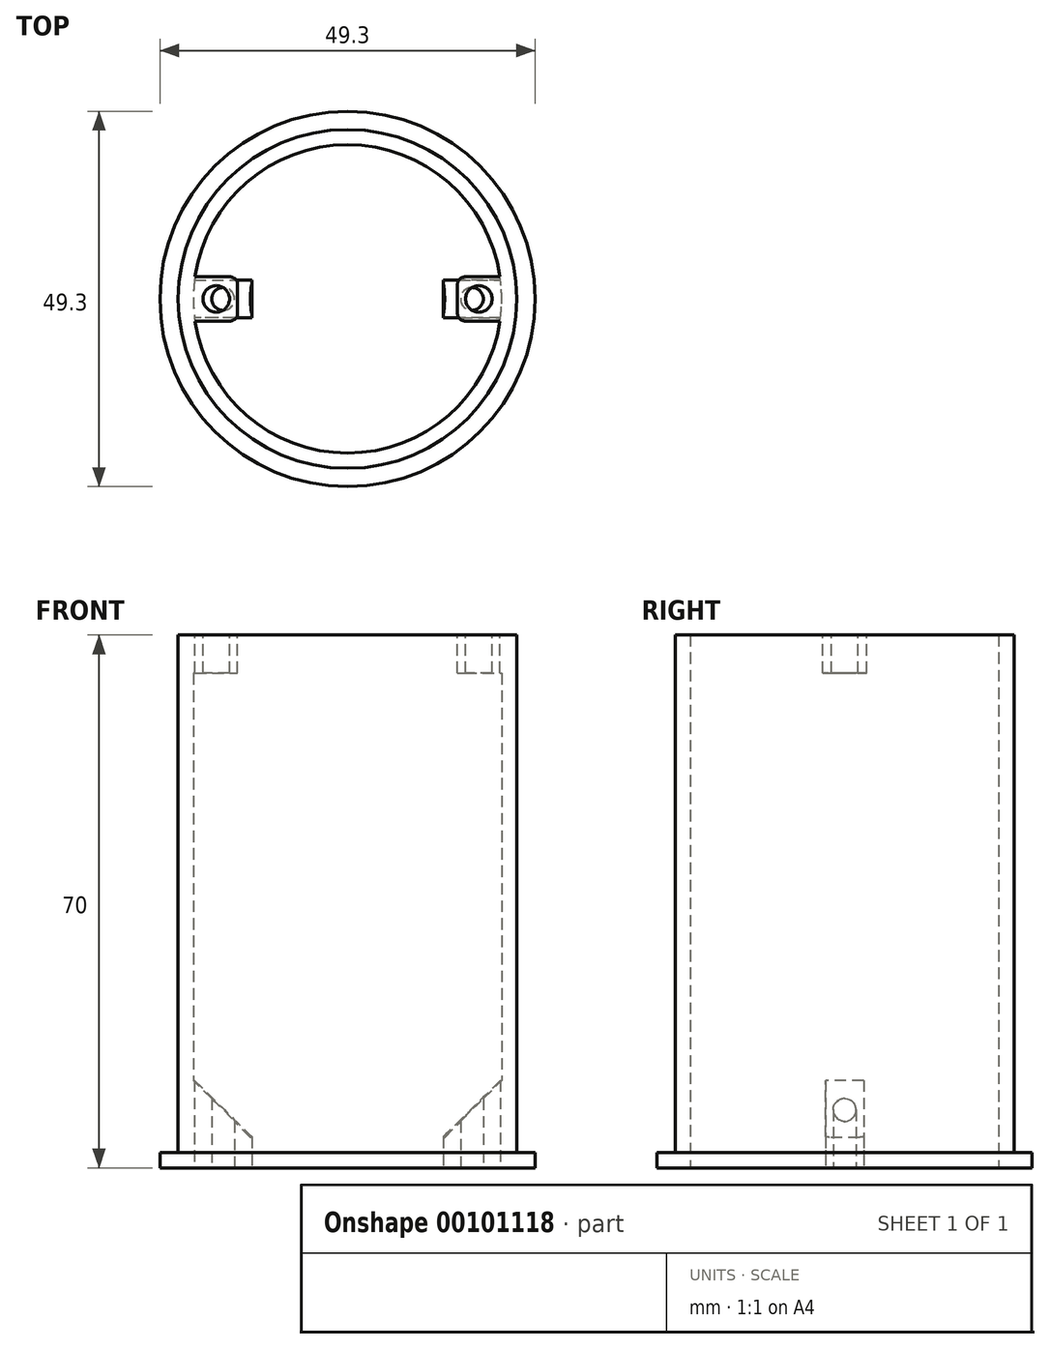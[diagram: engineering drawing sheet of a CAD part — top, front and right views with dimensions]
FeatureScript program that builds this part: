
annotation { "Feature Type Name" : "Feature", "Feature Type Description" : "" }
export const myFeature = defineFeature(function(context is Context, id is Id, definition is map)
    precondition{}
    {
        {
            var Q0;
            Q0=qCreatedBy(makeId("Top.planeOp"),FACE);
            var sketch = newSketch(context, id + "F0", { "sketchPlane" : qUnion([Q0])});
            skLineSegment(sketch, "E0.bottom", {"start": v(-4, 4) * mm, "end": v(4, 4) * mm});
            skLineSegment(sketch, "E0.top", {"start": v(-4, -4) * mm, "end": v(4, -4) * mm});
            skLineSegment(sketch, "E0.left", {"start": v(-4, 4) * mm, "end": v(-4, -4) * mm});
            skLineSegment(sketch, "E0.right", {"start": v(4, 4) * mm, "end": v(4, -4) * mm});
            skPoint(sketch, "E0.middle", {"position": v(0, 0) * mm});
            skLineSegment(sketch, "E1.bottom", {"start": v(-11, 11) * mm, "end": v(11, 11) * mm});
            skLineSegment(sketch, "E1.top", {"start": v(-11, -11) * mm, "end": v(11, -11) * mm});
            skLineSegment(sketch, "E1.left", {"start": v(-11, 11) * mm, "end": v(-11, -11) * mm});
            skLineSegment(sketch, "E1.right", {"start": v(11, 11) * mm, "end": v(11, -11) * mm});
            skCircle(sketch, "E2", {"center": v(0, 0) * mm, "radius": 10 * mm});
            skPoint(sketch, "E3", {"position": v(-7.5, 0) * mm});
            skPoint(sketch, "E3.positionSnap0", {"position": v(-11, 0) * mm});
            skCircle(sketch, "E4", {"center": v(-7.5, 0) * mm, "radius": 1.5 * mm});
            skPoint(sketch, "E5", {"position": v(7.5, 0) * mm});
            skPoint(sketch, "E5.positionSnap0", {"position": v(11, 0) * mm});
            skCircle(sketch, "E6", {"center": v(7.5, 0) * mm, "radius": 1.5 * mm});
            skCircle(sketch, "E7", {"center": v(0, 0) * mm, "radius": 22.25 * mm});
            skCircle(sketch, "E8", {"center": v(0, 0) * mm, "radius": 20.25 * mm});
            skSolve(sketch);
        }
        {
            var Q0;
            Q0=makeQuery(id+"F0.imprint","IMPRINT",FACE,{"disambiguationData":[TD([[makeQuery(id+"F0.imprint","IMPRINT",EDGE,{"derivedFrom":sQuery(id+"F0.wireOp",EDGE,"E7")}),1.0]])]});
            extrude(context, id + "F1", {"entities" : qUnion([Q0]), "depth" : 70 * mm});
        }
        {
            var Q0;
            Q0=makeQuery(id+"F1.opExtrude","CAP_FACE",FACE,{"disambiguationData":[OSD([sQuery(id+"F0.wireOp",EDGE,"E7"),sQuery(id+"F0.wireOp",EDGE,"E8")])],"isStart":false});
            cPlane(context, id + "F2", {"entities" : qUnion([Q0]), "cplaneType" : CPlaneType.OFFSET, "offset" : 0 * mm, "width" : 150 * mm, "height" : 150 * mm});
        }
        {
            var Q0;
            Q0=qCreatedBy(id+"F2.planeOp",FACE);
            var sketch = newSketch(context, id + "F3", { "sketchPlane" : qUnion([Q0])});
            skCircle(sketch, "E9", {"center": v(0, 0) * mm, "radius": 11.2 * mm});
            skCircle(sketch, "E10", {"center": v(0, 0) * mm, "radius": 20.25 * mm});
            skCircle(sketch, "E11", {"center": v(0, 0) * mm, "radius": 6.2 * mm});
            skSolve(sketch);
        }
        {
            var Q0;
            Q0=makeQuery(id+"F3.imprint","IMPRINT",FACE,{"disambiguationData":[TD([[makeQuery(id+"F3.imprint","IMPRINT",EDGE,{"derivedFrom":sQuery(id+"F3.wireOp",EDGE,"E10")}),1.0]])]});
            extrude(context, id + "F4", {"entities" : qUnion([Q0]), "oppositeDirection" : true, "depth" : 12 * mm});
        }
        {
            var Q0;
            Q0=makeQuery(id+"F3.imprint","IMPRINT",FACE,{"disambiguationData":[TD([[makeQuery(id+"F3.imprint","IMPRINT",EDGE,{"derivedFrom":sQuery(id+"F3.wireOp",EDGE,"E9")}),1.0]])]});
            extrude(context, id + "F5", {"entities" : qUnion([Q0]), "operationType" : NewBodyOperationType.ADD, "oppositeDirection" : true, "depth" : 4 * mm});
        }
        {
            var Q0;
            Q0=qCreatedBy(makeId("Top.planeOp"),FACE);
            var sketch = newSketch(context, id + "F6", { "sketchPlane" : qUnion([Q0])});
            skLineSegment(sketch, "E12", {"start": v(-20.1, 2.5) * mm, "end": v(-12.6, 2.5) * mm});
            skLineSegment(sketch, "E13", {"start": v(-12.6, 2.5) * mm, "end": v(-12.6, -2.5) * mm});
            skLineSegment(sketch, "E14", {"start": v(-12.6, -2.5) * mm, "end": v(-20.1, -2.5) * mm});
            skLineSegment(sketch, "E15", {"start": v(-20.1, -2.5) * mm, "end": v(-21.11, 0) * mm});
            skLineSegment(sketch, "E16", {"start": v(-21.11, 0) * mm, "end": v(-20.1, 2.5) * mm});
            skPoint(sketch, "E17", {"position": v(-16.35, 0) * mm});
            skPoint(sketch, "E17.positionSnap0", {"position": v(-12.6, 0) * mm});
            skPoint(sketch, "E17.positionSnap1", {"position": v(-16.35, 2.5) * mm});
            skCircle(sketch, "E18", {"center": v(-16.35, 0) * mm, "radius": 1.5 * mm});
            skLineSegment(sketch, "E19.MirrorCS", {"start": v(20.1, -2.5) * mm, "end": v(21.11, 0) * mm});
            skLineSegment(sketch, "E20.MirrorCS", {"start": v(21.11, 0) * mm, "end": v(20.1, 2.5) * mm});
            skLineSegment(sketch, "E21.MirrorCS", {"start": v(20.1, 2.5) * mm, "end": v(12.6, 2.5) * mm});
            skCircle(sketch, "E22.MirrorC", {"center": v(16.35, 0) * mm, "radius": 1.5 * mm});
            skLineSegment(sketch, "E23.MirrorCS", {"start": v(12.6, 2.5) * mm, "end": v(12.6, -2.5) * mm});
            skLineSegment(sketch, "E24.MirrorCS", {"start": v(12.6, -2.5) * mm, "end": v(20.1, -2.5) * mm});
            skSolve(sketch);
        }
        {
            var Q0;
            Q0=makeQuery(id+"F6.imprint","IMPRINT",FACE,{"disambiguationData":[TD([[makeQuery(id+"F6.imprint","IMPRINT",EDGE,{"derivedFrom":sQuery(id+"F6.wireOp",EDGE,"E12")}),-1.0]])]});
            var Q1;
            Q1=makeQuery(id+"F6.imprint","IMPRINT",FACE,{"disambiguationData":[TD([[makeQuery(id+"F6.imprint","IMPRINT",EDGE,{"derivedFrom":sQuery(id+"F6.wireOp",EDGE,"E19.MirrorCS")}),1.0]])]});
            extrude(context, id + "F7", {"entities" : qUnion([Q0, Q1]), "operationType" : NewBodyOperationType.ADD, "depth" : 4 * mm});
        }
        {
            var Q0;
            Q0=makeQuery(id+"F7.boolean.opBoolean","MERGE",FACE,{"derivedFrom":[makeQuery(id+"F1.opExtrude","CAP_FACE",FACE,{"disambiguationData":[OSD([sQuery(id+"F0.wireOp",EDGE,"E7"),sQuery(id+"F0.wireOp",EDGE,"E8")])],"isStart":true}),makeQuery(id+"F7.opExtrude","CAP_FACE",FACE,{"disambiguationData":[OSD([sQuery(id+"F6.wireOp",EDGE,"E12"),sQuery(id+"F6.wireOp",EDGE,"E13"),sQuery(id+"F6.wireOp",EDGE,"E14"),sQuery(id+"F6.wireOp",EDGE,"E15"),sQuery(id+"F6.wireOp",EDGE,"E16"),sQuery(id+"F6.wireOp",EDGE,"E18")])],"isStart":true}),makeQuery(id+"F7.opExtrude","CAP_FACE",FACE,{"disambiguationData":[OSD([sQuery(id+"F6.wireOp",EDGE,"E19.MirrorCS"),sQuery(id+"F6.wireOp",EDGE,"E20.MirrorCS"),sQuery(id+"F6.wireOp",EDGE,"E21.MirrorCS"),sQuery(id+"F6.wireOp",EDGE,"E22.MirrorC"),sQuery(id+"F6.wireOp",EDGE,"E23.MirrorCS"),sQuery(id+"F6.wireOp",EDGE,"E24.MirrorCS")])],"isStart":true})]});
            var sketch = newSketch(context, id + "F8", { "sketchPlane" : qUnion([Q0])});
            skCircle(sketch, "E25", {"center": v(0, 0) * mm, "radius": 24.65 * mm});
            skSolve(sketch);
        }
        {
            var Q0;
            Q0=makeQuery(id+"F8.imprint","IMPRINT",FACE,{"disambiguationData":[TD([[makeQuery(id+"F8.imprint","IMPRINT",EDGE,{"derivedFrom":sQuery(id+"F8.wireOp",EDGE,"E25")}),1.0]])]});
            extrude(context, id + "F9", {"entities" : qUnion([Q0]), "operationType" : NewBodyOperationType.ADD, "oppositeDirection" : true, "depth" : 2 * mm});
        }
        {
            var Q0;
            Q0=makeQuery(id+"F4.opExtrude","SWEPT_BODY",BODY,{"disambiguationData":[OSD([sQuery(id+"F3.wireOp",EDGE,"E9"),sQuery(id+"F3.wireOp",EDGE,"E10")])]});
            transform(context, id + "F10", {"entities" : qUnion([Q0]), "transformType" : TransformType.TRANSLATION_3D, "dx" : 0 * mm, "dy" : 0 * mm, "dz" : 0 * mm, "makeCopy" : true});
        }
        {
            var Q0;
            Q0=makeQuery(id+"F10.opPattern","COPY",BODY,{"derivedFrom":makeQuery(id+"F4.opExtrude","SWEPT_BODY",BODY,{"disambiguationData":[OSD([sQuery(id+"F3.wireOp",EDGE,"E9"),sQuery(id+"F3.wireOp",EDGE,"E10")])]}),"instanceName":"1"});
            deleteBodies(context, id + "F11", {"entities" : qUnion([Q0])});
        }
        {
            var Q0;
            Q0=makeQuery(id+"F4.opExtrude","SWEPT_BODY",BODY,{"disambiguationData":[OSD([sQuery(id+"F3.wireOp",EDGE,"E9"),sQuery(id+"F3.wireOp",EDGE,"E10")])]});
            deleteBodies(context, id + "F12", {"entities" : qUnion([Q0])});
        }
        {
            var Q0;
            Q0=makeQuery(id+"F1.opExtrude","CAP_FACE",FACE,{"disambiguationData":[OSD([sQuery(id+"F0.wireOp",EDGE,"E7"),sQuery(id+"F0.wireOp",EDGE,"E8")])],"isStart":false});
            var sketch = newSketch(context, id + "F13", { "sketchPlane" : qUnion([Q0])});
            skLineSegment(sketch, "E26", {"start": v(-20.04, 2.9) * mm, "end": v(-15.45, 2.9) * mm});
            skLineSegment(sketch, "E27", {"start": v(-14.45, 1.9) * mm, "end": v(-14.45, -1.9) * mm});
            skLineSegment(sketch, "E28", {"start": v(-15.45, -2.9) * mm, "end": v(-20.04, -2.9) * mm});
            skPoint(sketch, "E29.visualSharp", {"position": v(-14.45, 2.9) * mm});
            skArc(sketch, "E29.filletArc", {"start": v(-14.45, 1.9) * mm, "mid": v(-14.74, 2.6) * mm, "end": v(-15.45, 2.9) * mm});
            skPoint(sketch, "E30.visualSharp", {"position": v(-14.45, -2.9) * mm});
            skArc(sketch, "E30.filletArc", {"start": v(-15.45, -2.9) * mm, "mid": v(-14.74, -2.6) * mm, "end": v(-14.45, -1.9) * mm});
            skPoint(sketch, "E31", {"position": v(-17.25, 0) * mm});
            skLineSegment(sketch, "E32.MirrorCS", {"start": v(15.45, -2.9) * mm, "end": v(20.04, -2.9) * mm});
            skArc(sketch, "E33.MirrorCS", {"start": v(15.45, -2.9) * mm, "mid": v(14.74, -2.6) * mm, "end": v(14.45, -1.9) * mm});
            skPoint(sketch, "E34.MirrorP", {"position": v(17.25, 0) * mm});
            skLineSegment(sketch, "E35.MirrorCS", {"start": v(20.04, 2.9) * mm, "end": v(15.45, 2.9) * mm});
            skLineSegment(sketch, "E36.MirrorCS", {"start": v(14.45, 1.9) * mm, "end": v(14.45, -1.9) * mm});
            skArc(sketch, "E37.MirrorCS", {"start": v(14.45, 1.9) * mm, "mid": v(14.74, 2.6) * mm, "end": v(15.45, 2.9) * mm});
            skSolve(sketch);
        }
        {
            var Q0;
            {var subQ1=sQuery(id+"F13.wireOp",EDGE,"E26");Q0=makeQuery(id+"F13.imprint","IMPRINT",FACE,{"disambiguationData":[TD([[makeQuery(id+"F13.imprint","IMPRINT",EDGE,{"derivedFrom":subQ1}),-1.0]])]});}
            var Q1;
            {var subQ1=sQuery(id+"F13.wireOp",EDGE,"E32.MirrorCS");Q1=makeQuery(id+"F13.imprint","IMPRINT",FACE,{"disambiguationData":[TD([[makeQuery(id+"F13.imprint","IMPRINT",EDGE,{"derivedFrom":subQ1}),1.0]])]});}
            extrude(context, id + "F14", {"entities" : qUnion([Q0, Q1]), "operationType" : NewBodyOperationType.ADD, "oppositeDirection" : true, "depth" : 5 * mm});
        }
        {
            var Q0;
            Q0=sQuery(id+"F13.wireOp",VERTEX,"E31");
            var Q1;
            Q1=sQuery(id+"F13.wireOp",VERTEX,"E34.MirrorP");
            var Q2;
            Q2=makeQuery(id+"F1.opExtrude","SWEPT_BODY",BODY,{"disambiguationData":[OSD([sQuery(id+"F0.wireOp",EDGE,"E7"),sQuery(id+"F0.wireOp",EDGE,"E8")])]});
            hole(context, id + "F15", {"style" : HoleStyle.SIMPLE, "endStyle" : HoleEndStyle.BLIND, "holeDiameter" : 3.5 * mm, "holeDepth" : 25 * mm, "locations" : qUnion([Q0, Q1]), "scope" : qUnion([Q2])});
        }
        {
            var Q0;
            Q0=makeQuery(id+"F7.boolean.opBoolean","INTERSECT",EDGE,{"derivedFrom":[makeQuery(id+"F1.opExtrude","SWEPT_FACE",FACE,{"disambiguationData":[OSD([sQuery(id+"F0.wireOp",EDGE,"E8")])]}),makeQuery(id+"F7.opExtrude","CAP_FACE",FACE,{"disambiguationData":[OSD([sQuery(id+"F6.wireOp",EDGE,"E12"),sQuery(id+"F6.wireOp",EDGE,"E13"),sQuery(id+"F6.wireOp",EDGE,"E14"),sQuery(id+"F6.wireOp",EDGE,"E15"),sQuery(id+"F6.wireOp",EDGE,"E16"),sQuery(id+"F6.wireOp",EDGE,"E18")])],"isStart":false})]});
            var Q1;
            Q1=makeQuery(id+"F7.boolean.opBoolean","INTERSECT",EDGE,{"derivedFrom":[makeQuery(id+"F1.opExtrude","SWEPT_FACE",FACE,{"disambiguationData":[OSD([sQuery(id+"F0.wireOp",EDGE,"E8")])]}),makeQuery(id+"F7.opExtrude","CAP_FACE",FACE,{"disambiguationData":[OSD([sQuery(id+"F6.wireOp",EDGE,"E19.MirrorCS"),sQuery(id+"F6.wireOp",EDGE,"E20.MirrorCS"),sQuery(id+"F6.wireOp",EDGE,"E21.MirrorCS"),sQuery(id+"F6.wireOp",EDGE,"E22.MirrorC"),sQuery(id+"F6.wireOp",EDGE,"E23.MirrorCS"),sQuery(id+"F6.wireOp",EDGE,"E24.MirrorCS")])],"isStart":false})]});
            chamfer(context, id + "F16", {"entities" : qUnion([Q0, Q1]), "width" : 7.5 * mm, "tangentPropagation" : true});
        }
    });
